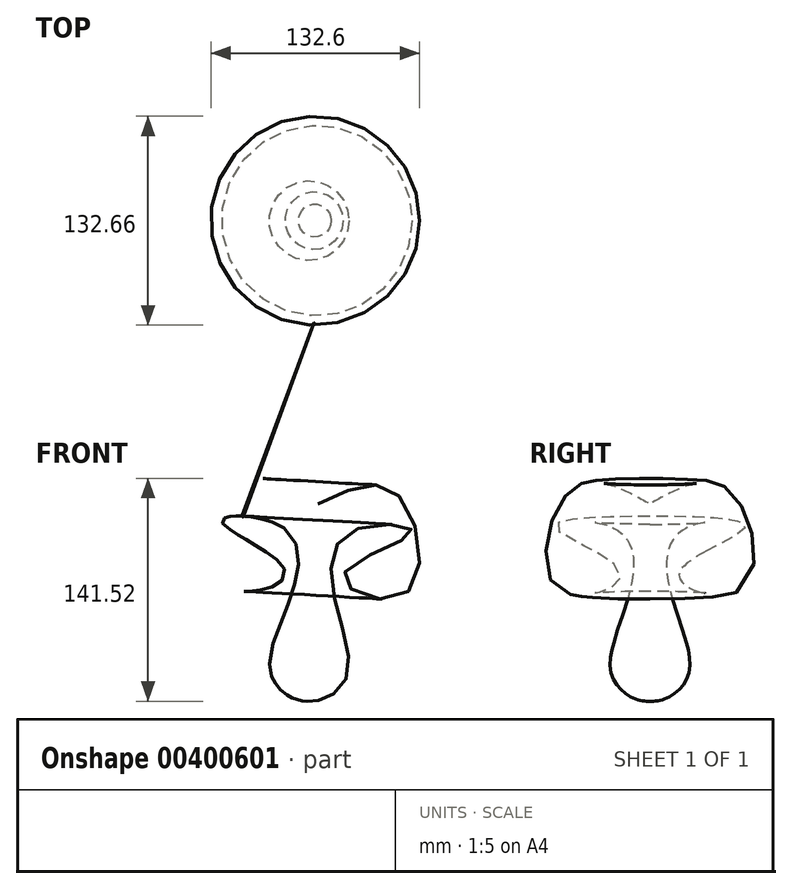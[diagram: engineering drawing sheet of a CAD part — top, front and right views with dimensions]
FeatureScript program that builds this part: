
annotation { "Feature Type Name" : "Feature", "Feature Type Description" : "" }
export const myFeature = defineFeature(function(context is Context, id is Id, definition is map)
    precondition{}
    {
        {
            var Q0;
            Q0=qCreatedBy(makeId("Front.planeOp"),FACE);
            var sketch = newSketch(context, id + "F0", { "sketchPlane" : qUnion([Q0])});
            skLineSegment(sketch, "E0", {"start": v(-26.79, 75.45) * mm, "end": v(-33.84, -49.95) * mm});
            skFitSpline(sketch, "E1", {"points": [v(-26.79, 75.45) * mm, v(23.26, 81.8) * mm, v(28.2, 18.01) * mm, v(-10.93, 29.63) * mm, v(32.78, 57.4) * mm, v(-5.29, 58.4) * mm, v(-16.92, 18.38) * mm, v(-8.1, -33.36) * mm, v(-24.32, -48.97) * mm, v(-33.84, -49.95) * mm], "startDerivative": vector(444.13, 216.55) * mm, "endDerivative": vector(-156.98, 7.91) * mm});
            skSolve(sketch);
        }
        {
            var Q0;
            Q0=makeQuery(id+"F0.imprint","IMPRINT",FACE,{"disambiguationData":[TD([[makeQuery(id+"F0.imprint","IMPRINT",EDGE,{"derivedFrom":sQuery(id+"F0.wireOp",EDGE,"E0")}),1.0]])]});
            var Q1;
            Q1=sQuery(id+"F0.wireOp",EDGE,"E0");
            revolve(context, id + "F1", {"entities" : qUnion([Q0]), "axis" : qUnion([Q1]), "revolveType" : RevolveType.FULL});
        }
    });
